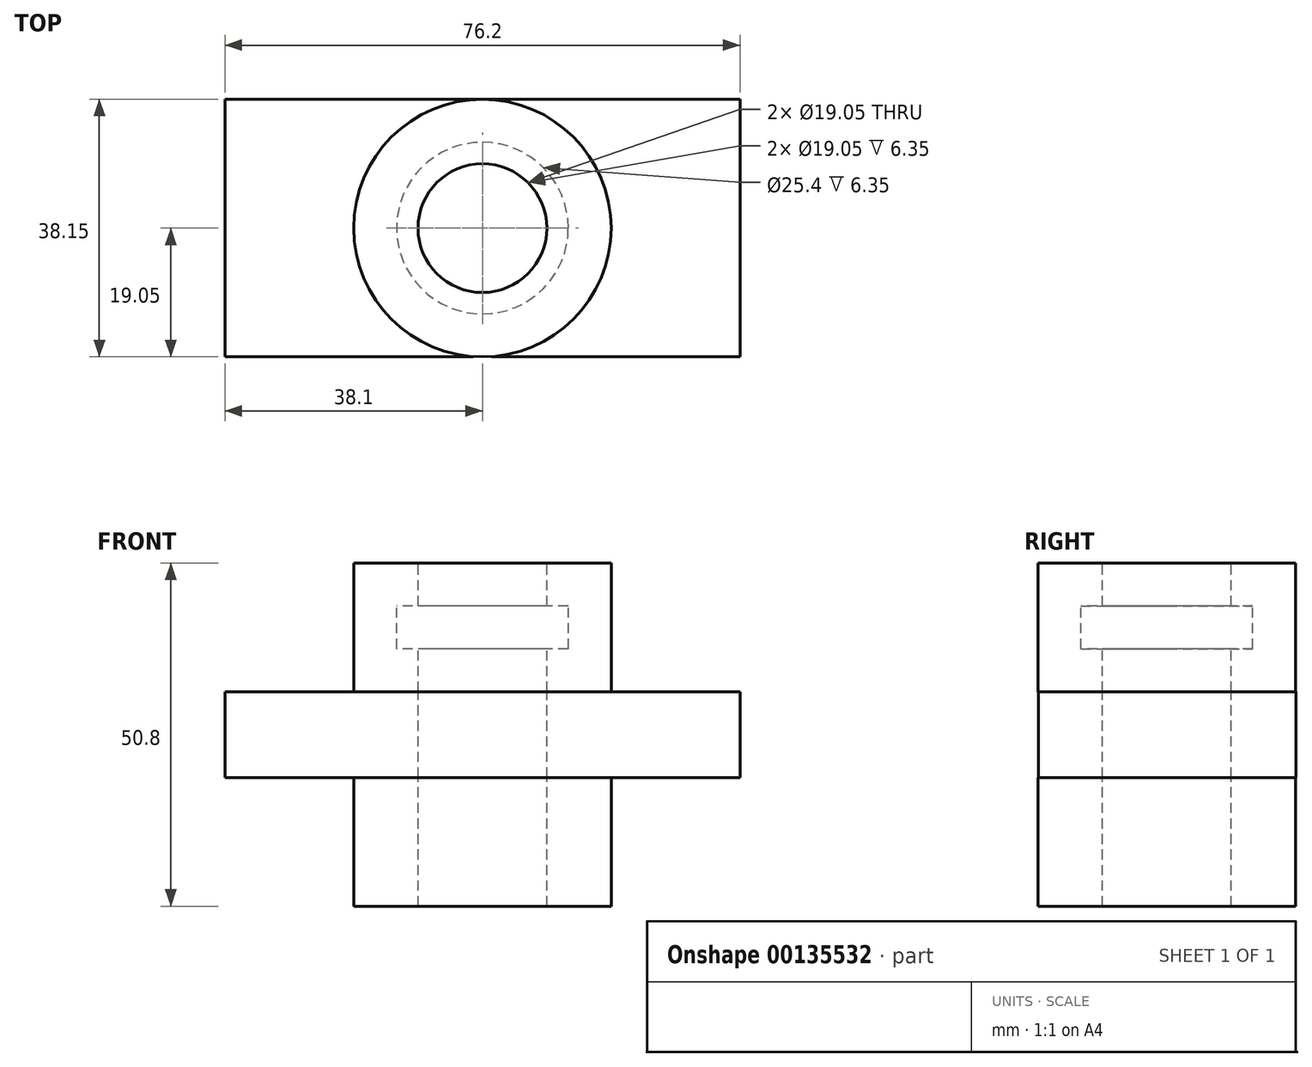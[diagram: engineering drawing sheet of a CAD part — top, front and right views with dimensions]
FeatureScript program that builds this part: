
annotation { "Feature Type Name" : "Feature", "Feature Type Description" : "" }
export const myFeature = defineFeature(function(context is Context, id is Id, definition is map)
    precondition{}
    {
        {
            var Q0;
            Q0=qCreatedBy(makeId("Front.planeOp"),FACE);
            var sketch = newSketch(context, id + "F0", { "sketchPlane" : qUnion([Q0])});
            skLineSegment(sketch, "E0", {"start": v(0, 0) * mm, "end": v(0, 12.7) * mm});
            skLineSegment(sketch, "E1", {"start": v(0, 12.7) * mm, "end": v(38.1, 12.7) * mm});
            skLineSegment(sketch, "E2", {"start": v(38.1, 12.7) * mm, "end": v(38.1, 0) * mm});
            skLineSegment(sketch, "E3", {"start": v(38.1, 0) * mm, "end": v(0, 0) * mm});
            skLineSegment(sketch, "E4", {"start": v(0, 12.7) * mm, "end": v(9.53, 12.7) * mm});
            skLineSegment(sketch, "E5", {"start": v(9.53, 12.7) * mm, "end": v(9.53, 19.05) * mm});
            skLineSegment(sketch, "E6", {"start": v(9.53, 19.05) * mm, "end": v(12.7, 19.05) * mm});
            skLineSegment(sketch, "E7", {"start": v(12.7, 19.05) * mm, "end": v(12.7, 25.4) * mm});
            skLineSegment(sketch, "E8", {"start": v(12.7, 25.4) * mm, "end": v(9.53, 25.4) * mm});
            skLineSegment(sketch, "E9", {"start": v(9.53, 25.4) * mm, "end": v(9.53, 31.75) * mm});
            skLineSegment(sketch, "E10", {"start": v(9.53, 31.75) * mm, "end": v(0, 31.75) * mm});
            skLineSegment(sketch, "E11", {"start": v(0, 12.7) * mm, "end": v(19.05, 12.7) * mm});
            skLineSegment(sketch, "E12", {"start": v(19.05, 12.7) * mm, "end": v(19.05, 31.75) * mm});
            skLineSegment(sketch, "E13", {"start": v(19.05, 31.75) * mm, "end": v(0, 31.75) * mm});
            skLineSegment(sketch, "E14", {"start": v(19.05, 0) * mm, "end": v(19.05, -19.05) * mm});
            skPoint(sketch, "E14.endSnap0", {"position": v(19.05, 0) * mm});
            skLineSegment(sketch, "E15", {"start": v(19.05, -19.05) * mm, "end": v(9.53, -19.05) * mm});
            skLineSegment(sketch, "E16", {"start": v(9.53, -19.05) * mm, "end": v(9.53, 0) * mm});
            skLineSegment(sketch, "E17", {"start": v(9.53, -19.05) * mm, "end": v(0, -19.05) * mm});
            skLineSegment(sketch, "E18", {"start": v(0, 46.1) * mm, "end": v(0, -36.78) * mm, "construction": true});
            skSolve(sketch);
        }
        {
            var Q0;
            {var subQ3=sQuery(id+"F0.wireOp",EDGE,"E5");Q0=makeQuery(id+"F0.imprint","IMPRINT",FACE,{"disambiguationData":[TD([[makeQuery(id+"F0.imprint","IMPRINT",EDGE,{"derivedFrom":subQ3}),-1.0]])]});}
            var Q1;
            {var subQ0=sQuery(id+"F0.wireOp",EDGE,"E14");Q1=makeQuery(id+"F0.imprint","IMPRINT",FACE,{"disambiguationData":[TD([[makeQuery(id+"F0.imprint","IMPRINT",EDGE,{"derivedFrom":subQ0}),-1.0]])]});}
            var Q2;
            Q2=sQuery(id+"F0.wireOp",EDGE,"E18");
            revolve(context, id + "F1", {"entities" : qUnion([Q0, Q1]), "axis" : qUnion([Q2]), "revolveType" : RevolveType.FULL});
        }
        {
            var Q0;
            Q0=qCreatedBy(makeId("Right.planeOp"),FACE);
            var sketch = newSketch(context, id + "F2", { "sketchPlane" : qUnion([Q0])});
            skLineSegment(sketch, "E19", {"start": v(0, 0) * mm, "end": v(19.1, 0) * mm});
            skLineSegment(sketch, "E20", {"start": v(19.1, 0) * mm, "end": v(19.1, 12.7) * mm});
            skLineSegment(sketch, "E21", {"start": v(19.1, 12.7) * mm, "end": v(-19, 12.7) * mm});
            skLineSegment(sketch, "E22", {"start": v(-19, 12.7) * mm, "end": v(-19, 0) * mm});
            skLineSegment(sketch, "E23", {"start": v(-19, 0) * mm, "end": v(0, 0) * mm});
            skSolve(sketch);
        }
        {
            var Q0;
            Q0 = qSketchRegion(id + "F2", true);
            extrude(context, id + "F3", {"entities" : qUnion([Q0]), "depth" : 38.1 * mm, "hasSecondDirection" : true, "secondDirectionOppositeDirection" : true, "secondDirectionDepth" : 38.1 * mm});
        }
        {
            var Q0;
            Q0=qCreatedBy(makeId("Top.planeOp"),FACE);
            var sketch = newSketch(context, id + "F4", { "sketchPlane" : qUnion([Q0])});
            skCircle(sketch, "E24", {"center": v(0, 0) * mm, "radius": 9.53 * mm});
            skSolve(sketch);
        }
        {
            var Q0;
            Q0 = qSketchRegion(id + "F4", true);
            extrude(context, id + "F5", {"entities" : qUnion([Q0]), "operationType" : NewBodyOperationType.REMOVE, "endBound" : BoundingType.THROUGH_ALL, "oppositeDirection" : true, "depth" : 25.4 * mm, "hasSecondDirection" : true, "secondDirectionOppositeDirection" : false, "secondDirectionDepth" : 80.42 * mm});
        }
    });
